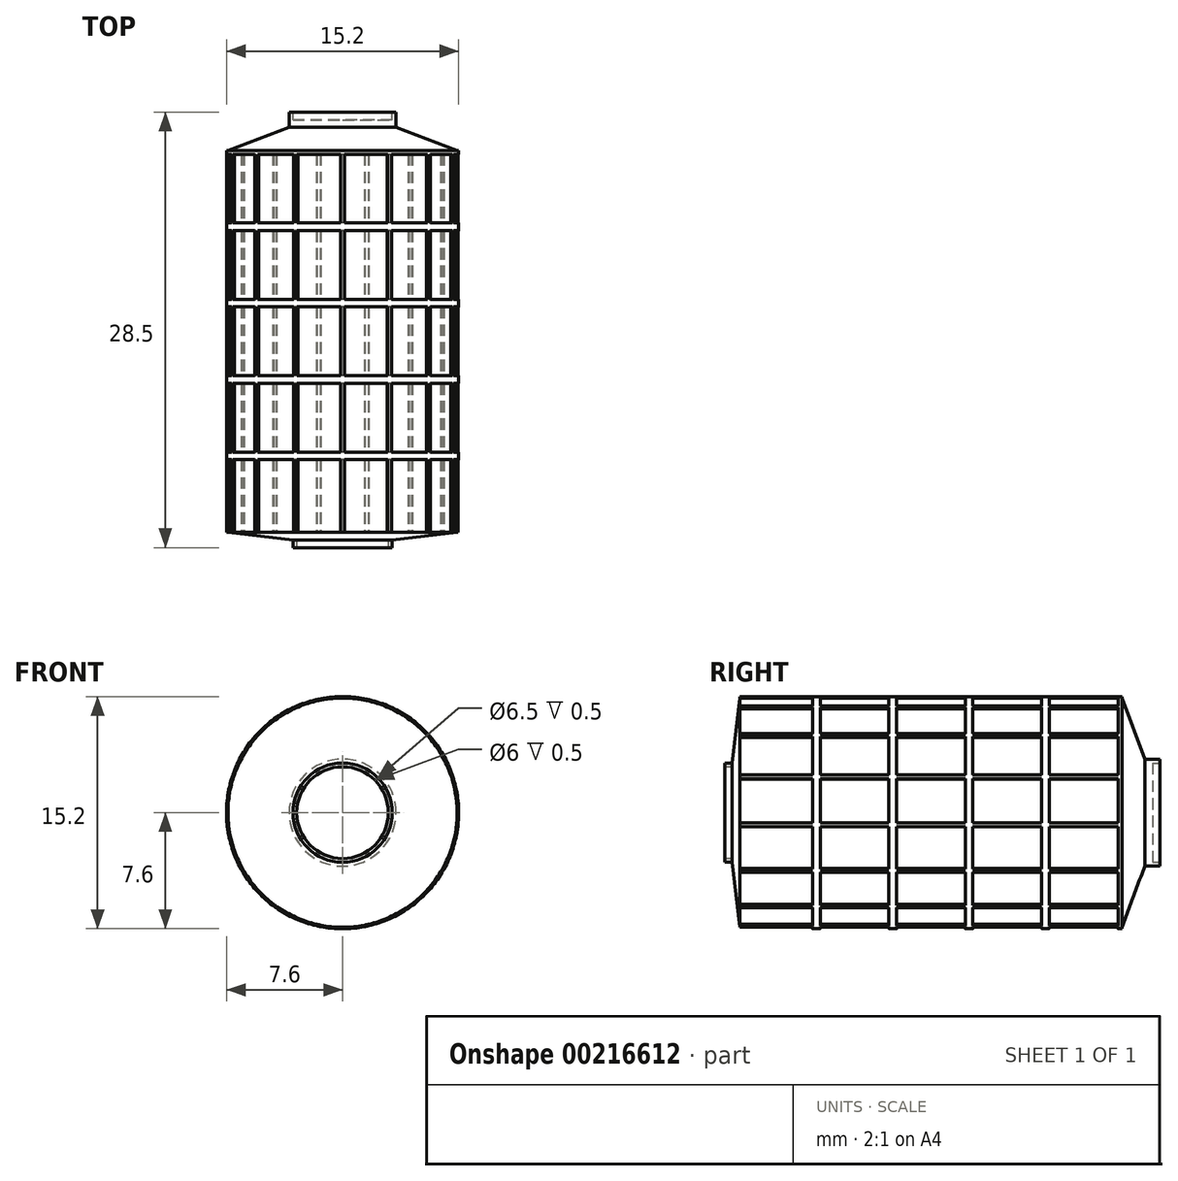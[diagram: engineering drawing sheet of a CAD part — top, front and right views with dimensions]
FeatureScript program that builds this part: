
annotation { "Feature Type Name" : "Feature", "Feature Type Description" : "" }
export const myFeature = defineFeature(function(context is Context, id is Id, definition is map)
    precondition{}
    {
        {
            var Q0;
            Q0=qCreatedBy(makeId("Front.planeOp"),FACE);
            var sketch = newSketch(context, id + "F0", { "sketchPlane" : qUnion([Q0])});
            skCircle(sketch, "E0", {"center": v(0, 0) * mm, "radius": 3.25 * mm});
            skSolve(sketch);
        }
        {
            var Q0;
            Q0=qCreatedBy(makeId("Front.planeOp"),FACE);
            cPlane(context, id + "F1", {"entities" : qUnion([Q0]), "cplaneType" : CPlaneType.OFFSET, "offset" : .5 * mm, "oppositeDirection" : true, "width" : 150 * mm, "height" : 150 * mm});
        }
        {
            var Q0;
            Q0=qCreatedBy(id+"F1.planeOp",FACE);
            var sketch = newSketch(context, id + "F2", { "sketchPlane" : qUnion([Q0])});
            skCircle(sketch, "E1", {"center": v(0, 0) * mm, "radius": 7.5 * mm});
            skSolve(sketch);
        }
        {
            var Q0;
            Q0=makeQuery(id+"F0.imprint","IMPRINT",FACE,{"disambiguationData":[TD([[makeQuery(id+"F0.imprint","IMPRINT",EDGE,{"derivedFrom":sQuery(id+"F0.wireOp",EDGE,"E0")}),1.0]])]});
            var Q1;
            Q1=makeQuery(id+"F2.imprint","IMPRINT",FACE,{"disambiguationData":[TD([[makeQuery(id+"F2.imprint","IMPRINT",EDGE,{"derivedFrom":sQuery(id+"F2.wireOp",EDGE,"E1")}),1.0]])]});
            loft(context, id + "F3", {"sheetProfilesArray" : [{ "sheetProfileEntities" : qUnion([Q0]) }, { "sheetProfileEntities" : qUnion([Q1]) }]});
        }
        {
            var Q0;
            Q0=makeQuery(id+"F3.opLoft","CAP_FACE",FACE,{"disambiguationData":[OSD([makeQuery(id+"F0.imprint","IMPRINT",FACE,{"disambiguationData":[TD([[makeQuery(id+"F0.imprint","IMPRINT",EDGE,{"derivedFrom":sQuery(id+"F0.wireOp",EDGE,"E0")}),1.0]])]})])],"isStart":true});
            extrude(context, id + "F4", {"entities" : qUnion([Q0]), "operationType" : NewBodyOperationType.ADD, "depth" : .5 * mm});
        }
        {
            var Q0;
            Q0=makeQuery(id+"F4.opExtrude","CAP_FACE",FACE,{"disambiguationData":[OSD([makeQuery(id+"F0.imprint","IMPRINT",FACE,{"disambiguationData":[TD([[makeQuery(id+"F0.imprint","IMPRINT",EDGE,{"derivedFrom":sQuery(id+"F0.wireOp",EDGE,"E0")}),1.0]])]})])],"isStart":false});
            var sketch = newSketch(context, id + "F5", { "sketchPlane" : qUnion([Q0])});
            skCircle(sketch, "E2", {"center": v(0, 0) * mm, "radius": 3 * mm});
            skSolve(sketch);
        }
        {
            var Q0;
            Q0=makeQuery(id+"F5.imprint","IMPRINT",FACE,{"disambiguationData":[TD([[makeQuery(id+"F5.imprint","IMPRINT",EDGE,{"derivedFrom":sQuery(id+"F5.wireOp",EDGE,"E2")}),1.0]])]});
            extrude(context, id + "F6", {"entities" : qUnion([Q0]), "operationType" : NewBodyOperationType.REMOVE, "oppositeDirection" : true, "depth" : .5 * mm});
        }
        {
            var Q0;
            Q0=makeQuery(id+"F3.opLoft","CAP_FACE",FACE,{"disambiguationData":[OSD([makeQuery(id+"F2.imprint","IMPRINT",FACE,{"disambiguationData":[TD([[makeQuery(id+"F2.imprint","IMPRINT",EDGE,{"derivedFrom":sQuery(id+"F2.wireOp",EDGE,"E1")}),1.0]])]})])],"isStart":true});
            extrude(context, id + "F7", {"entities" : qUnion([Q0]), "operationType" : NewBodyOperationType.ADD, "depth" : 25 * mm});
        }
        {
            var Q0;
            Q0=qCreatedBy(makeId("Front.planeOp"),FACE);
            cPlane(context, id + "F8", {"entities" : qUnion([Q0]), "cplaneType" : CPlaneType.OFFSET, "offset" : 27 * mm, "oppositeDirection" : true, "width" : 150 * mm, "height" : 150 * mm});
        }
        {
            var Q0;
            Q0=qCreatedBy(id+"F8.planeOp",FACE);
            var sketch = newSketch(context, id + "F9", { "sketchPlane" : qUnion([Q0])});
            skCircle(sketch, "E3", {"center": v(0, 0) * mm, "radius": 3.5 * mm});
            skSolve(sketch);
        }
        {
            var Q1;
            Q1=makeQuery(id+"F7.opExtrude","CAP_FACE",FACE,{"disambiguationData":[OSD([makeQuery(id+"F2.imprint","IMPRINT",FACE,{"disambiguationData":[TD([[makeQuery(id+"F2.imprint","IMPRINT",EDGE,{"derivedFrom":sQuery(id+"F2.wireOp",EDGE,"E1")}),1.0]])]})])],"isStart":false});
            var Q2;
            Q2=makeQuery(id+"F9.imprint","IMPRINT",FACE,{"disambiguationData":[TD([[makeQuery(id+"F9.imprint","IMPRINT",EDGE,{"derivedFrom":sQuery(id+"F9.wireOp",EDGE,"E3")}),1.0]])]});
            loft(context, id + "F10", {"operationType" : NewBodyOperationType.ADD, "sheetProfilesArray" : [{ "sheetProfileEntities" : qUnion([Q1]) }, { "sheetProfileEntities" : qUnion([Q2]) }]});
        }
        {
            var Q0;
            Q0=makeQuery(id+"F10.opLoft","CAP_FACE",FACE,{"disambiguationData":[OSD([makeQuery(id+"F9.imprint","IMPRINT",FACE,{"disambiguationData":[TD([[makeQuery(id+"F9.imprint","IMPRINT",EDGE,{"derivedFrom":sQuery(id+"F9.wireOp",EDGE,"E3")}),1.0]])]})])],"isStart":true});
            extrude(context, id + "F11", {"entities" : qUnion([Q0]), "operationType" : NewBodyOperationType.ADD, "depth" : 1 * mm});
        }
        {
            var Q0;
            Q0=makeQuery(id+"F11.opExtrude","CAP_FACE",FACE,{"disambiguationData":[OSD([makeQuery(id+"F9.imprint","IMPRINT",FACE,{"disambiguationData":[TD([[makeQuery(id+"F9.imprint","IMPRINT",EDGE,{"derivedFrom":sQuery(id+"F9.wireOp",EDGE,"E3")}),1.0]])]})])],"isStart":false});
            var sketch = newSketch(context, id + "F12", { "sketchPlane" : qUnion([Q0])});
            skCircle(sketch, "E4", {"center": v(0, 0) * mm, "radius": 3.25 * mm});
            skSolve(sketch);
        }
        {
            var Q0;
            Q0=makeQuery(id+"F12.imprint","IMPRINT",FACE,{"disambiguationData":[TD([[makeQuery(id+"F12.imprint","IMPRINT",EDGE,{"derivedFrom":sQuery(id+"F12.wireOp",EDGE,"E4")}),1.0]])]});
            extrude(context, id + "F13", {"entities" : qUnion([Q0]), "operationType" : NewBodyOperationType.REMOVE, "oppositeDirection" : true, "depth" : .5 * mm});
        }
        {
            var Q0;
            Q0=qCreatedBy(makeId("Right.planeOp"),FACE);
            var sketch = newSketch(context, id + "F14", { "sketchPlane" : qUnion([Q0])});
            skLineSegment(sketch, "E5", {"start": v(0, 0) * mm, "end": v(0, 7.5) * mm});
            skLineSegment(sketch, "E6", {"start": v(0, 7.5) * mm, "end": v(0.5, 7.5) * mm});
            skLineSegment(sketch, "E7", {"start": v(0.5, 7.5) * mm, "end": v(0.75, 7.5) * mm});
            skLineSegment(sketch, "E8", {"start": v(25.5, 7.5) * mm, "end": v(25.25, 7.5) * mm});
            skLineSegment(sketch, "E9", {"start": v(20.75, 7.5) * mm, "end": v(20.25, 7.5) * mm});
            skLineSegment(sketch, "E10", {"start": v(15.75, 7.5) * mm, "end": v(15.25, 7.5) * mm});
            skLineSegment(sketch, "E11", {"start": v(10.75, 7.5) * mm, "end": v(10.25, 7.5) * mm});
            skLineSegment(sketch, "E12", {"start": v(5.75, 7.5) * mm, "end": v(5.25, 7.5) * mm});
            skLineSegment(sketch, "E13", {"start": v(0.75, 7.5) * mm, "end": v(0.5, 7.5) * mm});
            skLineSegment(sketch, "E14", {"start": v(25.5, 7.5) * mm, "end": v(25.5, 7.6) * mm});
            skLineSegment(sketch, "E15", {"start": v(25.5, 7.6) * mm, "end": v(25.25, 7.6) * mm});
            skLineSegment(sketch, "E16", {"start": v(25.25, 7.6) * mm, "end": v(25.25, 7.5) * mm});
            skLineSegment(sketch, "E17", {"start": v(20.75, 7.5) * mm, "end": v(20.75, 7.6) * mm});
            skLineSegment(sketch, "E18", {"start": v(20.75, 7.6) * mm, "end": v(20.25, 7.6) * mm});
            skLineSegment(sketch, "E19", {"start": v(20.25, 7.6) * mm, "end": v(20.25, 7.5) * mm});
            skLineSegment(sketch, "E20.1.0.1", {"start": v(15.75, 7.6) * mm, "end": v(15.25, 7.6) * mm});
            skLineSegment(sketch, "E20.1.0.2", {"start": v(15.25, 7.6) * mm, "end": v(15.25, 7.5) * mm});
            skLineSegment(sketch, "E20.1.0.3", {"start": v(15.75, 7.5) * mm, "end": v(15.75, 7.6) * mm});
            skLineSegment(sketch, "E20.2.0.1", {"start": v(10.75, 7.6) * mm, "end": v(10.25, 7.6) * mm});
            skLineSegment(sketch, "E20.2.0.2", {"start": v(10.25, 7.6) * mm, "end": v(10.25, 7.5) * mm});
            skLineSegment(sketch, "E20.2.0.3", {"start": v(10.75, 7.5) * mm, "end": v(10.75, 7.6) * mm});
            skLineSegment(sketch, "E20.3.0.1", {"start": v(5.75, 7.6) * mm, "end": v(5.25, 7.6) * mm});
            skLineSegment(sketch, "E20.3.0.2", {"start": v(5.25, 7.6) * mm, "end": v(5.25, 7.5) * mm});
            skLineSegment(sketch, "E20.3.0.3", {"start": v(5.75, 7.5) * mm, "end": v(5.75, 7.6) * mm});
            skLineSegment(sketch, "E20.direction1", {"start": v(15.75, 7.5) * mm, "end": v(15.25, 7.5) * mm, "construction": true});
            skLineSegment(sketch, "E21", {"start": v(0.75, 7.5) * mm, "end": v(0.75, 7.6) * mm});
            skLineSegment(sketch, "E22", {"start": v(0.75, 7.6) * mm, "end": v(0.5, 7.6) * mm});
            skLineSegment(sketch, "E23", {"start": v(0.5, 7.6) * mm, "end": v(0.5, 7.5) * mm});
            skLineSegment(sketch, "E24.trimOffspring", {"start": v(15.25, 7.5) * mm, "end": v(15.75, 7.5) * mm});
            skLineSegment(sketch, "E25.trimOffspring", {"start": v(10.25, 7.5) * mm, "end": v(10.75, 7.5) * mm});
            skLineSegment(sketch, "E26.trimOffspring", {"start": v(5.25, 7.5) * mm, "end": v(5.75, 7.5) * mm});
            skLineSegment(sketch, "E27.trimOffspring", {"start": v(25.25, 7.5) * mm, "end": v(25.5, 7.5) * mm});
            skLineSegment(sketch, "E28.trimOffspring", {"start": v(20.25, 7.5) * mm, "end": v(20.75, 7.5) * mm});
            skSolve(sketch);
        }
        {
            var Q0;
            Q0=makeQuery(id+"F14.imprint","IMPRINT",FACE,{"disambiguationData":[TD([[makeQuery(id+"F14.imprint","IMPRINT",EDGE,{"derivedFrom":sQuery(id+"F14.wireOp",EDGE,"E14")}),1.0]])]});
            var Q1;
            Q1=makeQuery(id+"F14.imprint","IMPRINT",FACE,{"disambiguationData":[TD([[makeQuery(id+"F14.imprint","IMPRINT",EDGE,{"derivedFrom":sQuery(id+"F14.wireOp",EDGE,"E17")}),1.0]])]});
            var Q2;
            Q2=makeQuery(id+"F14.imprint","IMPRINT",FACE,{"disambiguationData":[TD([[makeQuery(id+"F14.imprint","IMPRINT",EDGE,{"derivedFrom":sQuery(id+"F14.wireOp",EDGE,"E13")}),-1.0]])]});
            var Q3;
            Q3=makeQuery(id+"F14.imprint","IMPRINT",FACE,{"disambiguationData":[TD([[makeQuery(id+"F14.imprint","IMPRINT",EDGE,{"derivedFrom":sQuery(id+"F14.wireOp",EDGE,"E20.2.0.1")}),1.0]])]});
            var Q4;
            Q4=makeQuery(id+"F14.imprint","IMPRINT",FACE,{"disambiguationData":[TD([[makeQuery(id+"F14.imprint","IMPRINT",EDGE,{"derivedFrom":sQuery(id+"F14.wireOp",EDGE,"E20.3.0.1")}),1.0]])]});
            var Q5;
            Q5=makeQuery(id+"F14.imprint","IMPRINT",FACE,{"disambiguationData":[TD([[makeQuery(id+"F14.imprint","IMPRINT",EDGE,{"derivedFrom":sQuery(id+"F14.wireOp",EDGE,"E20.1.0.1")}),1.0]])]});
            var Q6;
            {var subQ0=sQuery(id+"F2.wireOp",EDGE,"E1");var subQ1=sQuery(id+"F0.wireOp",EDGE,"E0");Q6=makeQuery(id+"F7.boolean.opBoolean","MERGE",EDGE,{"derivedFrom":[makeQuery(id+"F3.opLoft","MID_CAP_EDGE",EDGE,{"disambiguationData":[OSD([subQ1,subQ0])],"capPos":1.0}),makeQuery(id+"F7.opExtrude","CAP_EDGE",EDGE,{"disambiguationData":[OSD([subQ1,subQ0])],"isStart":true})]});}
            sweep(context, id + "F15", {"operationType" : NewBodyOperationType.ADD, "profiles" : qUnion([Q0, Q1, Q2, Q3, Q4, Q5]), "path" : qUnion([Q6])});
        }
        {
            var Q0;
            Q0=qCreatedBy(id+"F1.planeOp",FACE);
            var sketch = newSketch(context, id + "F16", { "sketchPlane" : qUnion([Q0])});
            skArc(sketch, "E29", {"start": v(0.13, 7.6) * mm, "mid": v(0, 7.6) * mm, "end": v(-0.13, 7.6) * mm});
            skArc(sketch, "E30", {"start": v(0.13, 7.5) * mm, "mid": v(0, 7.5) * mm, "end": v(-0.13, 7.5) * mm});
            skLineSegment(sketch, "E31", {"start": v(-0.13, 7.5) * mm, "end": v(-0.13, 7.6) * mm});
            skLineSegment(sketch, "E32", {"start": v(0.13, 7.5) * mm, "end": v(0.13, 7.6) * mm});
            skArc(sketch, "E33.1.0", {"start": v(-2.97, 7) * mm, "mid": v(-3.1, 6.94) * mm, "end": v(-3.21, 6.89) * mm});
            skLineSegment(sketch, "E33.1.1", {"start": v(-2.93, 6.9) * mm, "end": v(-2.97, 7) * mm});
            skLineSegment(sketch, "E33.1.2", {"start": v(-3.17, 6.8) * mm, "end": v(-3.21, 6.89) * mm});
            skArc(sketch, "E33.1.3", {"start": v(-2.93, 6.9) * mm, "mid": v(-3.05, 6.85) * mm, "end": v(-3.17, 6.8) * mm});
            skArc(sketch, "E33.2.0", {"start": v(-5.56, 5.18) * mm, "mid": v(-5.65, 5.09) * mm, "end": v(-5.74, 4.99) * mm});
            skLineSegment(sketch, "E33.2.1", {"start": v(-5.49, 5.11) * mm, "end": v(-5.56, 5.18) * mm});
            skLineSegment(sketch, "E33.2.2", {"start": v(-5.66, 4.92) * mm, "end": v(-5.74, 4.99) * mm});
            skArc(sketch, "E33.2.3", {"start": v(-5.49, 5.11) * mm, "mid": v(-5.57, 5.02) * mm, "end": v(-5.66, 4.92) * mm});
            skArc(sketch, "E33.3.0", {"start": v(-7.19, 2.47) * mm, "mid": v(-7.23, 2.35) * mm, "end": v(-7.27, 2.22) * mm});
            skLineSegment(sketch, "E33.3.1", {"start": v(-7.1, 2.44) * mm, "end": v(-7.19, 2.47) * mm});
            skLineSegment(sketch, "E33.3.2", {"start": v(-7.17, 2.2) * mm, "end": v(-7.27, 2.22) * mm});
            skArc(sketch, "E33.3.3", {"start": v(-7.1, 2.44) * mm, "mid": v(-7.13, 2.32) * mm, "end": v(-7.17, 2.2) * mm});
            skArc(sketch, "E33.4.0", {"start": v(-7.57, -0.66) * mm, "mid": v(-7.56, -0.8) * mm, "end": v(-7.54, -0.93) * mm});
            skLineSegment(sketch, "E33.4.1", {"start": v(-7.47, -0.65) * mm, "end": v(-7.57, -0.66) * mm});
            skLineSegment(sketch, "E33.4.2", {"start": v(-7.44, -0.91) * mm, "end": v(-7.54, -0.93) * mm});
            skArc(sketch, "E33.4.3", {"start": v(-7.47, -0.65) * mm, "mid": v(-7.46, -0.78) * mm, "end": v(-7.44, -0.91) * mm});
            skArc(sketch, "E33.5.0", {"start": v(-6.65, -3.68) * mm, "mid": v(-6.58, -3.8) * mm, "end": v(-6.51, -3.91) * mm});
            skLineSegment(sketch, "E33.5.1", {"start": v(-6.56, -3.64) * mm, "end": v(-6.65, -3.68) * mm});
            skLineSegment(sketch, "E33.5.2", {"start": v(-6.43, -3.86) * mm, "end": v(-6.51, -3.91) * mm});
            skArc(sketch, "E33.5.3", {"start": v(-6.56, -3.64) * mm, "mid": v(-6.5, -3.75) * mm, "end": v(-6.43, -3.86) * mm});
            skArc(sketch, "E33.6.0", {"start": v(-4.57, -6.07) * mm, "mid": v(-4.47, -6.15) * mm, "end": v(-4.36, -6.23) * mm});
            skLineSegment(sketch, "E33.6.1", {"start": v(-4.51, -5.99) * mm, "end": v(-4.57, -6.07) * mm});
            skLineSegment(sketch, "E33.6.2", {"start": v(-4.3, -6.14) * mm, "end": v(-4.36, -6.23) * mm});
            skArc(sketch, "E33.6.3", {"start": v(-4.51, -5.99) * mm, "mid": v(-4.4, -6.07) * mm, "end": v(-4.3, -6.14) * mm});
            skArc(sketch, "E33.7.0", {"start": v(-1.7, -7.4) * mm, "mid": v(-1.58, -7.43) * mm, "end": v(-1.45, -7.46) * mm});
            skLineSegment(sketch, "E33.7.1", {"start": v(-1.69, -7.3) * mm, "end": v(-1.7, -7.4) * mm});
            skLineSegment(sketch, "E33.7.2", {"start": v(-1.43, -7.36) * mm, "end": v(-1.45, -7.46) * mm});
            skArc(sketch, "E33.7.3", {"start": v(-1.69, -7.3) * mm, "mid": v(-1.56, -7.34) * mm, "end": v(-1.43, -7.36) * mm});
            skArc(sketch, "E33.8.0", {"start": v(1.45, -7.46) * mm, "mid": v(1.58, -7.43) * mm, "end": v(1.7, -7.4) * mm});
            skLineSegment(sketch, "E33.8.1", {"start": v(1.43, -7.36) * mm, "end": v(1.45, -7.46) * mm});
            skLineSegment(sketch, "E33.8.2", {"start": v(1.69, -7.3) * mm, "end": v(1.7, -7.4) * mm});
            skArc(sketch, "E33.8.3", {"start": v(1.43, -7.36) * mm, "mid": v(1.56, -7.34) * mm, "end": v(1.69, -7.3) * mm});
            skArc(sketch, "E33.9.0", {"start": v(4.36, -6.23) * mm, "mid": v(4.47, -6.15) * mm, "end": v(4.57, -6.07) * mm});
            skLineSegment(sketch, "E33.9.1", {"start": v(4.3, -6.14) * mm, "end": v(4.36, -6.23) * mm});
            skLineSegment(sketch, "E33.9.2", {"start": v(4.51, -5.99) * mm, "end": v(4.57, -6.07) * mm});
            skArc(sketch, "E33.9.3", {"start": v(4.3, -6.14) * mm, "mid": v(4.4, -6.07) * mm, "end": v(4.51, -5.99) * mm});
            skArc(sketch, "E33.10.0", {"start": v(6.51, -3.91) * mm, "mid": v(6.58, -3.8) * mm, "end": v(6.65, -3.68) * mm});
            skLineSegment(sketch, "E33.10.1", {"start": v(6.43, -3.86) * mm, "end": v(6.51, -3.91) * mm});
            skLineSegment(sketch, "E33.10.2", {"start": v(6.56, -3.64) * mm, "end": v(6.65, -3.68) * mm});
            skArc(sketch, "E33.10.3", {"start": v(6.43, -3.86) * mm, "mid": v(6.5, -3.75) * mm, "end": v(6.56, -3.64) * mm});
            skArc(sketch, "E33.11.0", {"start": v(7.54, -0.93) * mm, "mid": v(7.56, -0.8) * mm, "end": v(7.57, -0.66) * mm});
            skLineSegment(sketch, "E33.11.1", {"start": v(7.44, -0.91) * mm, "end": v(7.54, -0.93) * mm});
            skLineSegment(sketch, "E33.11.2", {"start": v(7.47, -0.65) * mm, "end": v(7.57, -0.66) * mm});
            skArc(sketch, "E33.11.3", {"start": v(7.44, -0.91) * mm, "mid": v(7.46, -0.78) * mm, "end": v(7.47, -0.65) * mm});
            skArc(sketch, "E33.12.0", {"start": v(7.27, 2.22) * mm, "mid": v(7.23, 2.35) * mm, "end": v(7.19, 2.47) * mm});
            skLineSegment(sketch, "E33.12.1", {"start": v(7.17, 2.2) * mm, "end": v(7.27, 2.22) * mm});
            skLineSegment(sketch, "E33.12.2", {"start": v(7.1, 2.44) * mm, "end": v(7.19, 2.47) * mm});
            skArc(sketch, "E33.12.3", {"start": v(7.17, 2.2) * mm, "mid": v(7.13, 2.32) * mm, "end": v(7.1, 2.44) * mm});
            skArc(sketch, "E33.13.0", {"start": v(5.74, 4.99) * mm, "mid": v(5.65, 5.09) * mm, "end": v(5.56, 5.18) * mm});
            skLineSegment(sketch, "E33.13.1", {"start": v(5.66, 4.92) * mm, "end": v(5.74, 4.99) * mm});
            skLineSegment(sketch, "E33.13.2", {"start": v(5.49, 5.11) * mm, "end": v(5.56, 5.18) * mm});
            skArc(sketch, "E33.13.3", {"start": v(5.66, 4.92) * mm, "mid": v(5.57, 5.02) * mm, "end": v(5.49, 5.11) * mm});
            skArc(sketch, "E33.14.0", {"start": v(3.21, 6.89) * mm, "mid": v(3.1, 6.94) * mm, "end": v(2.97, 7) * mm});
            skLineSegment(sketch, "E33.14.1", {"start": v(3.17, 6.8) * mm, "end": v(3.21, 6.89) * mm});
            skLineSegment(sketch, "E33.14.2", {"start": v(2.93, 6.9) * mm, "end": v(2.97, 7) * mm});
            skArc(sketch, "E33.14.3", {"start": v(3.17, 6.8) * mm, "mid": v(3.05, 6.85) * mm, "end": v(2.93, 6.9) * mm});
            skSolve(sketch);
        }
        {
            var Q0;
            Q0 = qSketchRegion(id + "F16", true);
            extrude(context, id + "F17", {"entities" : qUnion([Q0]), "operationType" : NewBodyOperationType.ADD, "oppositeDirection" : true, "depth" : 25 * mm});
        }
    });
